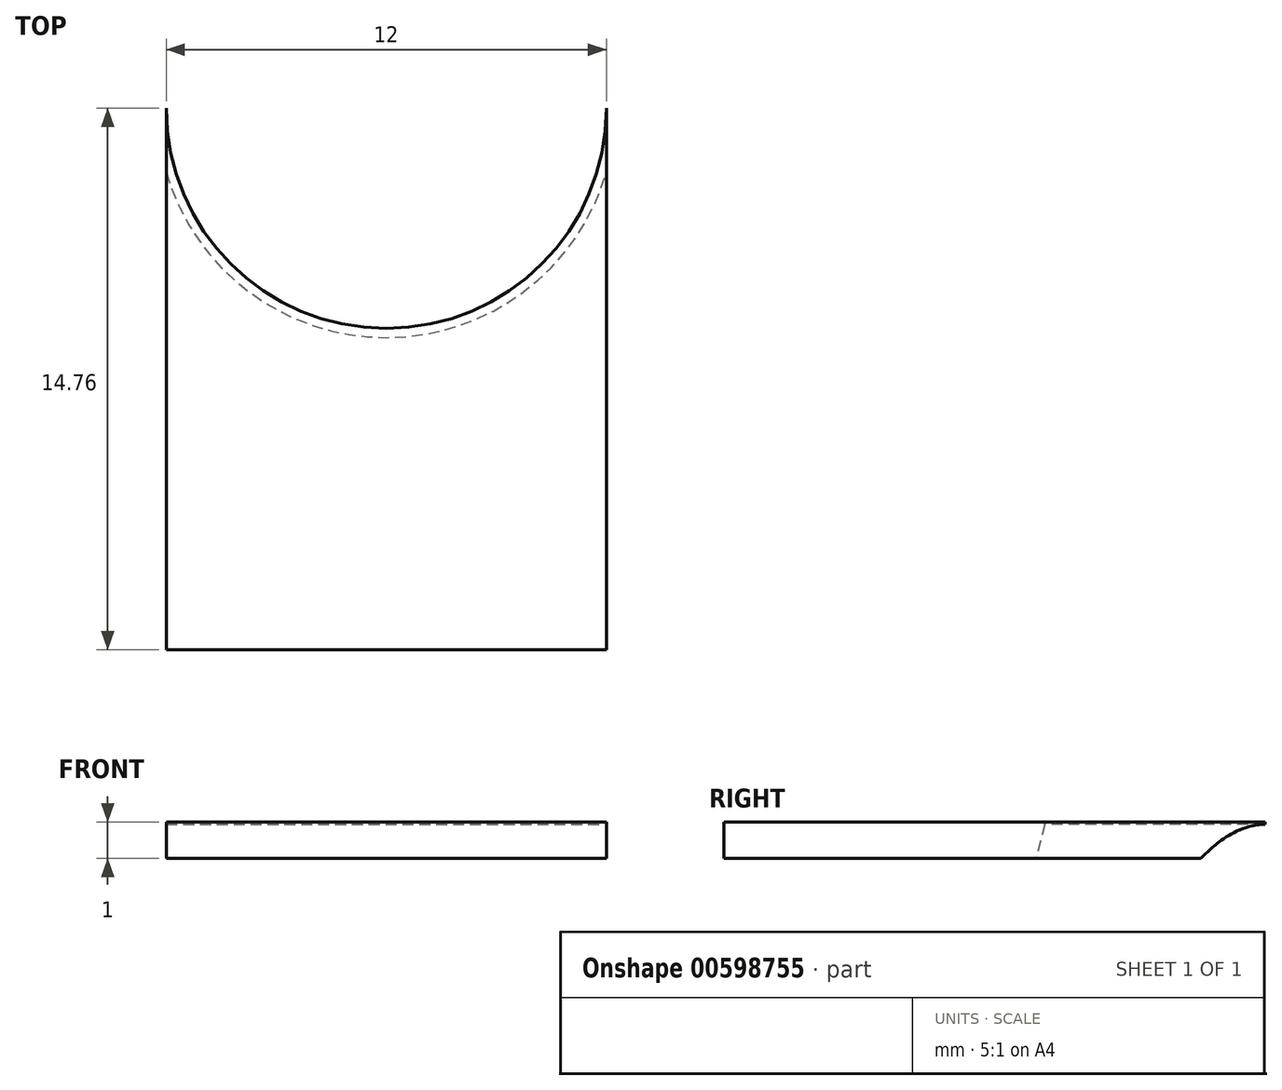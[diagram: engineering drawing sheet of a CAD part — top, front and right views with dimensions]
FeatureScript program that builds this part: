
annotation { "Feature Type Name" : "Feature", "Feature Type Description" : "" }
export const myFeature = defineFeature(function(context is Context, id is Id, definition is map)
    precondition{}
    {
        {
            var Q0;
            Q0=qCreatedBy(makeId("Top.planeOp"),FACE);
            var sketch = newSketch(context, id + "F0", { "sketchPlane" : qUnion([Q0])});
            skLineSegment(sketch, "E0.bottom", {"start": v(-6, 7.38) * mm, "end": v(6, 7.38) * mm});
            skLineSegment(sketch, "E0.top", {"start": v(-6, -7.38) * mm, "end": v(6, -7.38) * mm});
            skLineSegment(sketch, "E0.left", {"start": v(-6, 7.38) * mm, "end": v(-6, -7.38) * mm});
            skLineSegment(sketch, "E0.right", {"start": v(6, 7.38) * mm, "end": v(6, -7.38) * mm});
            skPoint(sketch, "E0.middle", {"position": v(0, 0) * mm});
            skSolve(sketch);
        }
        {
            var Q0;
            Q0=makeQuery(id+"F0.imprint","IMPRINT",FACE,{"disambiguationData":[TD([[makeQuery(id+"F0.imprint","IMPRINT",EDGE,{"derivedFrom":sQuery(id+"F0.wireOp",EDGE,"E0.bottom")}),-1.0]])]});
            extrude(context, id + "F1", {"entities" : qUnion([Q0]), "depth" : 1 * mm, "offsetDistance" : 25.4 * mm});
        }
        {
            var Q0;
            Q0=makeQuery(id+"F1.opExtrude","CAP_FACE",FACE,{"disambiguationData":[OSD([sQuery(id+"F0.wireOp",EDGE,"E0.bottom"),sQuery(id+"F0.wireOp",EDGE,"E0.top"),sQuery(id+"F0.wireOp",EDGE,"E0.left"),sQuery(id+"F0.wireOp",EDGE,"E0.right")])],"isStart":false});
            var sketch = newSketch(context, id + "F2", { "sketchPlane" : qUnion([Q0])});
            skCircle(sketch, "E1", {"center": v(0, 7.38) * mm, "radius": 6 * mm});
            skSolve(sketch);
        }
        {
            var Q0;
            {var subQ1=makeQuery(id+"F1.opExtrude","CAP_EDGE",EDGE,{"disambiguationData":[OSD([sQuery(id+"F0.wireOp",EDGE,"E0.bottom")])],"isStart":false});Q0=makeQuery(id+"F2.imprint","IMPRINT",FACE,{"disambiguationData":[TD([[makeQuery(id+"F2.imprint","IMPRINT",EDGE,{"derivedFrom":subQ1}),-1.0]])]});}
            extrude(context, id + "F3", {"entities" : qUnion([Q0]), "operationType" : NewBodyOperationType.REMOVE, "oppositeDirection" : true, "depth" : 25.4 * mm, "offsetDistance" : 25.4 * mm, "hasSecondDirection" : true, "secondDirectionOppositeDirection" : false, "secondDirectionDepth" : 25.4 * mm});
        }
        {
            var Q0;
            Q0=makeQuery(id+"F3.boolean.opBoolean","INTERSECT",EDGE,{"derivedFrom":[makeQuery(id+"F1.opExtrude","CAP_FACE",FACE,{"disambiguationData":[OSD([sQuery(id+"F0.wireOp",EDGE,"E0.bottom"),sQuery(id+"F0.wireOp",EDGE,"E0.top"),sQuery(id+"F0.wireOp",EDGE,"E0.left"),sQuery(id+"F0.wireOp",EDGE,"E0.right")])],"isStart":true}),makeQuery(id+"F3.opExtrude","SWEPT_FACE",FACE,{"disambiguationData":[OSD([sQuery(id+"F2.wireOp",EDGE,"E1")])]})]});
            chamfer(context, id + "F4", {"entities" : qUnion([Q0]), "chamferType" : ChamferType.OFFSET_ANGLE, "width" : .25 * mm, "oppositeDirection" : false, "angle" : 75 * degree, "tangentPropagation" : true});
        }
    });
